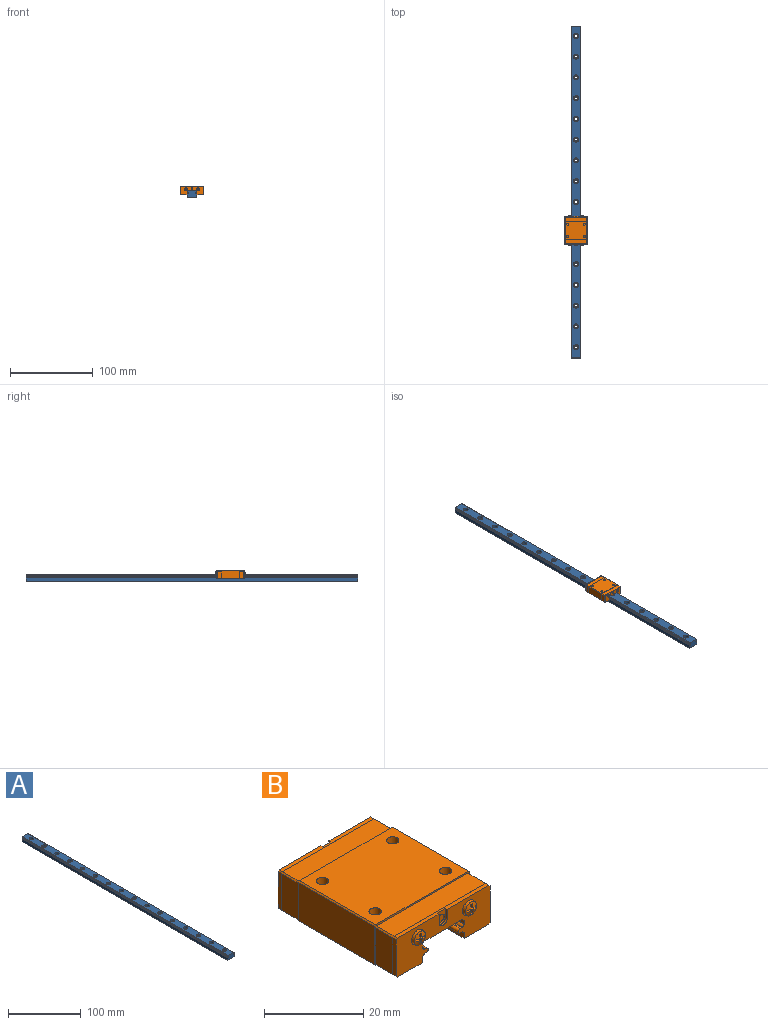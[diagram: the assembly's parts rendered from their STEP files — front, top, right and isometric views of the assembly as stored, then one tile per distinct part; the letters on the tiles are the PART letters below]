
ASSEMBLY  parts=2 mates=1
PART A: 76 faces, bbox 12x400x8 mm
  f0: cylinder r=1.75mm len=5mm, axis (0,0,1), area 55mm2, adj f17,f74
  f1: cylinder r=1.75mm len=5mm, axis (0,0,1), area 55mm2, adj f17,f72
  f2: cylinder r=1.75mm len=5mm, axis (0,0,1), area 55mm2, adj f17,f70
  f3: cylinder r=1.75mm len=5mm, axis (0,0,1), area 55mm2, adj f17,f68
  f4: cylinder r=1.75mm len=5mm, axis (0,0,1), area 55mm2, adj f17,f66
  f5: cylinder r=1.75mm len=5mm, axis (0,0,1), area 55mm2, adj f17,f64
  f6: cylinder r=1.75mm len=5mm, axis (0,0,1), area 55mm2, adj f17,f62
  f7: cylinder r=1.75mm len=5mm, axis (0,0,1), area 55mm2, adj f17,f60
  f8: cylinder r=1.75mm len=5mm, axis (0,0,1), area 55mm2, adj f17,f58
  f9: cylinder r=1.75mm len=5mm, axis (0,0,1), area 55mm2, adj f17,f56
  f10: cylinder r=1.75mm len=5mm, axis (0,0,1), area 55mm2, adj f17,f54
  f11: cylinder r=1.75mm len=5mm, axis (0,0,1), area 55mm2, adj f17,f52
  f12: cylinder r=1.75mm len=5mm, axis (0,0,1), area 55mm2, adj f17,f50
  f13: cylinder r=1.75mm len=5mm, axis (0,0,1), area 55mm2, adj f17,f48
  f14: cylinder r=1.75mm len=5mm, axis (0,0,1), area 55mm2, adj f17,f46
  f15: cylinder r=1.75mm len=5mm, axis (0,0,1), area 55mm2, adj f17,f44
  f16: plane 400x4.32mm, normal (-1,0,0), area 1728.7mm2, adj f17,f32,f33,f43
  f17: plane 400x12mm, normal (0,0,-1), area 4646.1mm2, adj f0,f1,f2,f3,f4,f5,f6,f7
  f18: plane 400x4.32mm, normal (1,0,0), area 1728.7mm2, adj f17,f32,f33,f36
  f19: cylinder r=1.14mm len=400mm, axis (0,1,0), area 250.4mm2, adj f32,f33,f36,f37
  f20: plane 400x0.42mm, normal (0,0,1), area 169.7mm2, adj f21,f32,f33,f37
  f21: cylinder r=0.5mm len=400mm, axis (0,1,0), area 754.1mm2, adj f20,f22,f32,f33
  f22: plane 400x0.42mm, normal (0,0,-1), area 168.4mm2, adj f21,f32,f33,f38
  f23: cylinder r=1.14mm len=400mm, axis (0,1,0), area 250.7mm2, adj f32,f33,f38,f39
  f24: plane 400x0.91mm, normal (1,0,0), area 363.9mm2, adj f32,f33,f35,f39
  f25: plane 400x11mm, normal (0,0,1), area 3947.6mm2, adj f32,f33,f34,f35,f45,f47,f49,f51
  f26: plane 400x0.91mm, normal (-1,0,0), area 363.9mm2, adj f32,f33,f34,f40
  f27: cylinder r=1.14mm len=400mm, axis (0,1,0), area 250.7mm2, adj f32,f33,f40,f41
  f28: plane 400x0.42mm, normal (0,0,-1), area 168.4mm2, adj f29,f32,f33,f41
  f29: cylinder r=0.5mm len=400mm, axis (0,1,0), area 754.1mm2, adj f28,f30,f32,f33
  f30: plane 400x0.42mm, normal (0,0,1), area 169.7mm2, adj f29,f32,f33,f42
  f31: cylinder r=1.14mm len=400mm, axis (0,1,0), area 250.4mm2, adj f32,f33,f42,f43
  f32: plane 12x8mm, normal (0,-1,0), area 91.8mm2, adj f16,f17,f18,f19,f20,f21,f22,f23
  f33: plane 12x8mm, normal (0,1,0), area 91.8mm2, adj f16,f17,f18,f19,f20,f21,f22,f23
  f34: plane 400x0.5mm, normal (-0.71,0,0.71), area 282.8mm2, adj f25,f26,f32,f33
  f35: plane 400x0.5mm, normal (0.71,0,0.71), area 282.8mm2, adj f24,f25,f32,f33
  f36: cylinder r=0.16mm len=400mm, axis (0,1,0), area 67.9mm2, adj f18,f19,f32,f33
  f37: cylinder r=0.16mm len=400mm, axis (0,1,0), area 67.8mm2, adj f19,f20,f32,f33
  f38: cylinder r=0.16mm len=400mm, axis (0,1,0), area 67.9mm2, adj f22,f23,f32,f33
  f39: cylinder r=0.16mm len=400mm, axis (0,1,0), area 67.9mm2, adj f23,f24,f32,f33
  f40: cylinder r=0.16mm len=400mm, axis (0,1,0), area 67.9mm2, adj f26,f27,f32,f33
  f41: cylinder r=0.16mm len=400mm, axis (0,1,0), area 67.9mm2, adj f27,f28,f32,f33
  f42: cylinder r=0.16mm len=400mm, axis (0,1,0), area 67.8mm2, adj f30,f31,f32,f33
  f43: cylinder r=0.16mm len=400mm, axis (0,1,0), area 67.9mm2, adj f16,f31,f32,f33
  f44: plane 6x6mm, normal (0,0,1), area 18.7mm2, adj f15,f45
  f45: cylinder r=3mm len=6mm, axis (0,0,1), area 56.5mm2, adj f25,f44
  f46: plane 6x6mm, normal (0,0,1), area 18.7mm2, adj f14,f47
  f47: cylinder r=3mm len=6mm, axis (0,0,1), area 56.5mm2, adj f25,f46
  f48: plane 6x6mm, normal (0,0,1), area 18.7mm2, adj f13,f49
  f49: cylinder r=3mm len=6mm, axis (0,0,1), area 56.5mm2, adj f25,f48
  f50: plane 6x6mm, normal (0,0,1), area 18.7mm2, adj f12,f51
  f51: cylinder r=3mm len=6mm, axis (0,0,1), area 56.5mm2, adj f25,f50
  f52: plane 6x6mm, normal (0,0,1), area 18.7mm2, adj f11,f53
  f53: cylinder r=3mm len=6mm, axis (0,0,1), area 56.5mm2, adj f25,f52
  f54: plane 6x6mm, normal (0,0,1), area 18.7mm2, adj f10,f55
  f55: cylinder r=3mm len=6mm, axis (0,0,1), area 56.5mm2, adj f25,f54
  f56: plane 6x6mm, normal (0,0,1), area 18.7mm2, adj f9,f57
  f57: cylinder r=3mm len=6mm, axis (0,0,1), area 56.5mm2, adj f25,f56
  f58: plane 6x6mm, normal (0,0,1), area 18.7mm2, adj f8,f59
  f59: cylinder r=3mm len=6mm, axis (0,0,1), area 56.5mm2, adj f25,f58
  f60: plane 6x6mm, normal (0,0,1), area 18.7mm2, adj f7,f61
  f61: cylinder r=3mm len=6mm, axis (0,0,1), area 56.5mm2, adj f25,f60
  f62: plane 6x6mm, normal (0,0,1), area 18.7mm2, adj f6,f63
  f63: cylinder r=3mm len=6mm, axis (0,0,1), area 56.5mm2, adj f25,f62
  f64: plane 6x6mm, normal (0,0,1), area 18.7mm2, adj f5,f65
  f65: cylinder r=3mm len=6mm, axis (0,0,1), area 56.5mm2, adj f25,f64
  f66: plane 6x6mm, normal (0,0,1), area 18.7mm2, adj f4,f67
  f67: cylinder r=3mm len=6mm, axis (0,0,1), area 56.5mm2, adj f25,f66
  f68: plane 6x6mm, normal (0,0,1), area 18.7mm2, adj f3,f69
  f69: cylinder r=3mm len=6mm, axis (0,0,1), area 56.5mm2, adj f25,f68
  f70: plane 6x6mm, normal (0,0,1), area 18.7mm2, adj f2,f71
  f71: cylinder r=3mm len=6mm, axis (0,0,1), area 56.5mm2, adj f25,f70
  f72: plane 6x6mm, normal (0,0,1), area 18.7mm2, adj f1,f73
  f73: cylinder r=3mm len=6mm, axis (0,0,1), area 56.5mm2, adj f25,f72
  f74: plane 6x6mm, normal (0,0,1), area 18.7mm2, adj f0,f75
  f75: cylinder r=3mm len=6mm, axis (0,0,1), area 56.5mm2, adj f25,f74
PART B: 172 faces, bbox 27x35.9x10 mm
  f0: cylinder r=1.25mm len=3.5mm, axis (0,0,-1), area 27.5mm2, adj f1,f158
  f1: cone r=0.62mm half-angle=59deg, axis (0,0,1), area 5.7mm2, adj f0
  f2: cylinder r=1.25mm len=3.5mm, axis (0,0,-1), area 27.5mm2, adj f3,f158
  f3: cone r=0.62mm half-angle=59deg, axis (0,0,1), area 5.7mm2, adj f2
  f4: cylinder r=1.25mm len=3.5mm, axis (0,0,-1), area 27.5mm2, adj f5,f158
  f5: cone r=0.62mm half-angle=59deg, axis (0,0,1), area 5.7mm2, adj f4
  f6: cylinder r=1.25mm len=3.5mm, axis (0,0,-1), area 27.5mm2, adj f7,f158
  f7: cone r=0.62mm half-angle=59deg, axis (0,0,1), area 5.7mm2, adj f6
  f8: cylinder r=0.5mm len=33.7mm, axis (0,1,0), area 63.6mm2, adj f58,f115,f148,f149
  f9: cylinder r=0.5mm len=33.7mm, axis (0,1,0), area 63.6mm2, adj f58,f115,f137,f138
  f10: cylinder r=1.15mm len=2.3mm, axis (0,1,0), area 3.6mm2, adj f114,f124
  f11: cylinder r=1.75mm len=3.5mm, axis (0,1,0), area 5.5mm2, adj f109,f115
  f12: cylinder r=1.75mm len=3.5mm, axis (0,1,0), area 5.5mm2, adj f108,f115
  f13: cone r=0.85mm half-angle=5deg, axis (0,1,0), area 11.5mm2, adj f14,f109
  f14: cone r=0.8mm half-angle=72.7deg, axis (0,1,0), area 6.3mm2, adj f13,f96,f97,f98,f99,f100,f101,f102
  f15: cone r=0.85mm half-angle=5deg, axis (0,1,0), area 11.5mm2, adj f16,f108
  f16: cone r=0.8mm half-angle=72.7deg, axis (0,1,0), area 6.3mm2, adj f15,f83,f84,f85,f86,f87,f88,f89
  f17: cylinder r=1.15mm len=2.3mm, axis (0,-1,0), area 3.6mm2, adj f57,f67
  f18: cylinder r=1.75mm len=3.5mm, axis (0,-1,0), area 5.5mm2, adj f52,f58
  f19: cylinder r=1.75mm len=3.5mm, axis (0,-1,0), area 5.5mm2, adj f51,f58
  f20: cone r=0.85mm half-angle=5deg, axis (0,-1,0), area 11.5mm2, adj f21,f52
  f21: cone r=0.8mm half-angle=72.7deg, axis (0,-1,0), area 6.3mm2, adj f20,f39,f40,f41,f42,f43,f44,f45
  f22: cone r=0.85mm half-angle=5deg, axis (0,-1,0), area 11.5mm2, adj f23,f51
  f23: cone r=0.8mm half-angle=72.7deg, axis (0,-1,0), area 6.3mm2, adj f22,f26,f27,f28,f29,f30,f31,f32
  f24: plane 26.6x9.6mm, normal (0,-1,0), area 0.3mm2, adj f55,f59,f60,f61,f62,f63,f64,f65
  f25: plane 2.4x2.4mm, normal (0,1,0), area 2.1mm2, adj f26,f27,f28,f29,f30,f31,f32,f33
  f26: plane 0.93x0.49mm, normal (0,0,1), area 0.4mm2, adj f23,f25,f29,f31
  f27: plane 0.93x0.49mm, normal (0,0,-1), area 0.4mm2, adj f23,f25,f28,f30
  f28: plane 1.36x1.29mm, normal (-1,0,0), area 1mm2, adj f23,f25,f27,f36
  f29: plane 1.36x1.29mm, normal (-1,0,0), area 1mm2, adj f23,f25,f26,f32
  f30: plane 1.36x1.29mm, normal (1,0,0), area 1mm2, adj f23,f25,f27,f33
  f31: plane 1.36x1.29mm, normal (1,0,0), area 1mm2, adj f23,f25,f26,f34
  f32: plane 1.36x1.29mm, normal (0,0,1), area 1mm2, adj f23,f25,f29,f35
  f33: plane 1.36x1.29mm, normal (0,0,-1), area 1mm2, adj f23,f25,f30,f37
  f34: plane 1.36x1.29mm, normal (0,0,1), area 1mm2, adj f23,f25,f31,f37
  f35: plane 0.93x0.49mm, normal (-1,0,0), area 0.4mm2, adj f23,f25,f32,f36
  f36: plane 1.36x1.29mm, normal (0,0,-1), area 1mm2, adj f23,f25,f28,f35
  f37: plane 0.94x0.49mm, normal (1,0,0), area 0.4mm2, adj f23,f25,f33,f34
  f38: plane 2.4x2.4mm, normal (0,1,0), area 2.1mm2, adj f39,f40,f41,f42,f43,f44,f45,f46
  f39: plane 0.93x0.49mm, normal (0,0,1), area 0.4mm2, adj f21,f38,f42,f44
  f40: plane 0.93x0.49mm, normal (0,0,-1), area 0.4mm2, adj f21,f38,f41,f43
  f41: plane 1.36x1.29mm, normal (-1,0,0), area 1mm2, adj f21,f38,f40,f49
  f42: plane 1.36x1.29mm, normal (-1,0,0), area 1mm2, adj f21,f38,f39,f45
  f43: plane 1.36x1.29mm, normal (1,0,0), area 1mm2, adj f21,f38,f40,f46
  f44: plane 1.36x1.29mm, normal (1,0,0), area 1mm2, adj f21,f38,f39,f47
  f45: plane 1.36x1.29mm, normal (0,0,1), area 1mm2, adj f21,f38,f42,f48
  f46: plane 1.36x1.29mm, normal (0,0,-1), area 1mm2, adj f21,f38,f43,f50
  f47: plane 1.36x1.29mm, normal (0,0,1), area 1mm2, adj f21,f38,f44,f50
  f48: plane 0.93x0.49mm, normal (-1,0,0), area 0.4mm2, adj f21,f38,f45,f49
  f49: plane 1.36x1.29mm, normal (0,0,-1), area 1mm2, adj f21,f38,f41,f48
  f50: plane 0.94x0.49mm, normal (1,0,0), area 0.4mm2, adj f21,f38,f46,f47
  f51: plane 3.5x3.5mm, normal (0,1,0), area 0.5mm2, adj f19,f22
  f52: plane 3.5x3.5mm, normal (0,1,0), area 0.5mm2, adj f18,f20
  f53: plane 2.1x0.5mm, normal (1,0,0), area 1.1mm2, adj f55,f56,f57,f58
  f54: plane 2.1x0.5mm, normal (-1,0,0), area 1.1mm2, adj f55,f56,f57,f58
  f55: plane 26x1mm, normal (0,0,1), area 24.8mm2, adj f24,f53,f54,f57,f58,f62,f63
  f56: cylinder r=1.2mm len=2.4mm, axis (0,-1,0), area 1.9mm2, adj f53,f54,f57,f58
  f57: plane 3.3x2.4mm, normal (0,1,0), area 3.1mm2, adj f17,f53,f54,f55,f56
  f58: plane 26.6x9.6mm, normal (0,1,0), area 172.9mm2, adj f8,f9,f18,f19,f53,f54,f55,f56
  f59: plane 7x1mm, normal (0,0,-1), area 7mm2, adj f24,f58,f65,f134
  f60: plane 7x1mm, normal (0,0,-1), area 7mm2, adj f24,f58,f66,f152
  f61: plane 9x1mm, normal (1,0,0), area 9mm2, adj f24,f58,f62,f66
  f62: plane 1x0.3mm, normal (0.71,0,0.71), area 0.4mm2, adj f24,f55,f58,f61
  f63: plane 1x0.3mm, normal (-0.71,0,0.71), area 0.4mm2, adj f24,f55,f58,f64
  f64: plane 9x1mm, normal (-1,0,0), area 9mm2, adj f24,f58,f63,f65
  f65: plane 1x0.3mm, normal (-0.71,0,-0.71), area 0.4mm2, adj f24,f58,f59,f64
  f66: plane 1x0.3mm, normal (0.71,0,-0.71), area 0.4mm2, adj f24,f58,f60,f61
  f67: plane 2.3x2.3mm, normal (0,1,0), area 4.2mm2, adj f17
  f68: cylinder r=1.14mm len=33.7mm, axis (0,-1,0), area 21.1mm2, adj f58,f115,f150,f151
  f69: cylinder r=1.14mm len=33.7mm, axis (0,-1,0), area 21.1mm2, adj f58,f115,f146,f147
  f70: cylinder r=1.14mm len=33.7mm, axis (0,-1,0), area 21.1mm2, adj f58,f115,f139,f140
  f71: cylinder r=1.14mm len=33.7mm, axis (0,-1,0), area 21.1mm2, adj f58,f115,f135,f136
  f72: plane 7x5mm, normal (0,0,-1), area 35mm2, adj f24,f79,f134,f163
  f73: plane 7x5mm, normal (0,0,-1), area 35mm2, adj f24,f80,f152,f163
  f74: plane 8.99x5mm, normal (1,0,0), area 45mm2, adj f24,f75,f80,f163
  f75: plane 5x0.3mm, normal (0.71,0,0.71), area 2.1mm2, adj f24,f74,f76,f163
  f76: plane 25.99x5mm, normal (0,0,1), area 130mm2, adj f24,f75,f77,f163
  f77: plane 5x0.3mm, normal (-0.71,0,0.71), area 2.1mm2, adj f24,f76,f78,f163
  f78: plane 8.99x5mm, normal (-1,0,0), area 45mm2, adj f24,f77,f79,f163
  f79: plane 5x0.3mm, normal (-0.71,0,-0.71), area 2.1mm2, adj f24,f72,f78,f163
  f80: plane 5x0.3mm, normal (0.71,0,-0.71), area 2.1mm2, adj f24,f73,f74,f163
  f81: plane 26.6x9.6mm, normal (0,1,0), area 0.3mm2, adj f112,f116,f117,f118,f119,f120,f121,f122
  f82: plane 2.4x2.4mm, normal (0,-1,0), area 2.1mm2, adj f83,f84,f85,f86,f87,f88,f89,f90
  f83: plane 0.93x0.49mm, normal (0,0,1), area 0.4mm2, adj f16,f82,f86,f88
  f84: plane 0.93x0.49mm, normal (0,0,-1), area 0.4mm2, adj f16,f82,f85,f87
  f85: plane 1.36x1.29mm, normal (1,0,0), area 1mm2, adj f16,f82,f84,f93
  f86: plane 1.36x1.29mm, normal (1,0,0), area 1mm2, adj f16,f82,f83,f89
  f87: plane 1.36x1.29mm, normal (-1,0,0), area 1mm2, adj f16,f82,f84,f90
  f88: plane 1.36x1.29mm, normal (-1,0,0), area 1mm2, adj f16,f82,f83,f91
  f89: plane 1.36x1.29mm, normal (0,0,1), area 1mm2, adj f16,f82,f86,f92
  f90: plane 1.36x1.29mm, normal (0,0,-1), area 1mm2, adj f16,f82,f87,f94
  f91: plane 1.36x1.29mm, normal (0,0,1), area 1mm2, adj f16,f82,f88,f94
  f92: plane 0.93x0.49mm, normal (1,0,0), area 0.4mm2, adj f16,f82,f89,f93
  f93: plane 1.36x1.29mm, normal (0,0,-1), area 1mm2, adj f16,f82,f85,f92
  f94: plane 0.94x0.49mm, normal (-1,0,0), area 0.4mm2, adj f16,f82,f90,f91
  f95: plane 2.4x2.4mm, normal (0,-1,0), area 2.1mm2, adj f96,f97,f98,f99,f100,f101,f102,f103
  f96: plane 0.93x0.49mm, normal (0,0,1), area 0.4mm2, adj f14,f95,f99,f101
  f97: plane 0.93x0.49mm, normal (0,0,-1), area 0.4mm2, adj f14,f95,f98,f100
  f98: plane 1.36x1.29mm, normal (1,0,0), area 1mm2, adj f14,f95,f97,f106
  f99: plane 1.36x1.29mm, normal (1,0,0), area 1mm2, adj f14,f95,f96,f102
  f100: plane 1.36x1.29mm, normal (-1,0,0), area 1mm2, adj f14,f95,f97,f103
  f101: plane 1.36x1.29mm, normal (-1,0,0), area 1mm2, adj f14,f95,f96,f104
  f102: plane 1.36x1.29mm, normal (0,0,1), area 1mm2, adj f14,f95,f99,f105
  f103: plane 1.36x1.29mm, normal (0,0,-1), area 1mm2, adj f14,f95,f100,f107
  f104: plane 1.36x1.29mm, normal (0,0,1), area 1mm2, adj f14,f95,f101,f107
  f105: plane 0.93x0.49mm, normal (1,0,0), area 0.4mm2, adj f14,f95,f102,f106
  f106: plane 1.36x1.29mm, normal (0,0,-1), area 1mm2, adj f14,f95,f98,f105
  f107: plane 0.94x0.49mm, normal (-1,0,0), area 0.4mm2, adj f14,f95,f103,f104
  f108: plane 3.5x3.5mm, normal (0,-1,0), area 0.5mm2, adj f12,f15
  f109: plane 3.5x3.5mm, normal (0,-1,0), area 0.5mm2, adj f11,f13
  f110: plane 2.1x0.5mm, normal (-1,0,0), area 1mm2, adj f112,f113,f114,f115
  f111: plane 2.1x0.5mm, normal (1,0,0), area 1mm2, adj f112,f113,f114,f115
  f112: plane 26x1mm, normal (0,0,1), area 24.8mm2, adj f81,f110,f111,f114,f115,f119,f120
  f113: cylinder r=1.2mm len=2.4mm, axis (0,1,0), area 1.9mm2, adj f110,f111,f114,f115
  f114: plane 3.3x2.4mm, normal (0,-1,0), area 3.1mm2, adj f10,f110,f111,f112,f113
  f115: plane 26.6x9.6mm, normal (0,-1,0), area 172.9mm2, adj f8,f9,f11,f12,f68,f69,f70,f71
  f116: plane 7x1mm, normal (0,0,-1), area 7mm2, adj f81,f115,f122,f152
  f117: plane 7x1mm, normal (0,0,-1), area 7mm2, adj f81,f115,f123,f134
  f118: plane 9x1mm, normal (-1,0,0), area 9mm2, adj f81,f115,f119,f123
  f119: plane 1x0.3mm, normal (-0.71,0,0.71), area 0.4mm2, adj f81,f112,f115,f118
  f120: plane 1x0.3mm, normal (0.71,0,0.71), area 0.4mm2, adj f81,f112,f115,f121
  f121: plane 9x1mm, normal (1,0,0), area 9mm2, adj f81,f115,f120,f122
  f122: plane 1x0.3mm, normal (0.71,0,-0.71), area 0.4mm2, adj f81,f115,f116,f121
  f123: plane 1x0.3mm, normal (-0.71,0,-0.71), area 0.4mm2, adj f81,f115,f117,f118
  f124: plane 2.3x2.3mm, normal (0,-1,0), area 4.2mm2, adj f10
  f125: plane 7x5mm, normal (0,0,-1), area 35mm2, adj f81,f132,f152,f153
  f126: plane 7x5mm, normal (0,0,-1), area 35mm2, adj f81,f133,f134,f153
  f127: plane 8.99x5mm, normal (-1,0,0), area 44.9mm2, adj f81,f128,f133,f153
  f128: plane 5x0.3mm, normal (-0.71,0,0.71), area 2.1mm2, adj f81,f127,f129,f153
  f129: plane 25.99x5mm, normal (0,0,1), area 129.9mm2, adj f81,f128,f130,f153
  f130: plane 5x0.3mm, normal (0.71,0,0.71), area 2.1mm2, adj f81,f129,f131,f153
  f131: plane 8.99x5mm, normal (1,0,0), area 45mm2, adj f81,f130,f132,f153
  f132: plane 5x0.3mm, normal (0.71,0,-0.71), area 2.1mm2, adj f81,f125,f131,f153
  f133: plane 5x0.3mm, normal (-0.71,0,-0.71), area 2.1mm2, adj f81,f126,f127,f153
  f134: plane 33.7x1.32mm, normal (1,0,0), area 44.5mm2, adj f24,f58,f59,f72,f81,f115,f117,f126
  f135: cylinder r=0.16mm len=33.7mm, axis (0,1,0), area 5.7mm2, adj f58,f71,f115,f134
  f136: cylinder r=0.16mm len=33.7mm, axis (0,1,0), area 5.7mm2, adj f58,f71,f115,f137
  f137: plane 33.7x0.42mm, normal (0,0,-1), area 14.2mm2, adj f9,f58,f115,f136
  f138: plane 33.7x0.42mm, normal (0,0,1), area 14.2mm2, adj f9,f58,f115,f139
  f139: cylinder r=0.16mm len=33.7mm, axis (0,1,0), area 5.7mm2, adj f58,f70,f115,f138
  f140: cylinder r=0.16mm len=33.7mm, axis (0,1,0), area 5.7mm2, adj f58,f70,f115,f141
  f141: plane 33.7x0.82mm, normal (1,0,0), area 27.7mm2, adj f58,f115,f140,f142
  f142: plane 33.7x0.59mm, normal (0.76,0,-0.65), area 26mm2, adj f58,f115,f141,f143
  f143: plane 33.7x11mm, normal (0,0,-1), area 370.7mm2, adj f58,f115,f142,f144
  f144: plane 33.7x0.59mm, normal (-0.76,0,-0.65), area 26mm2, adj f58,f115,f143,f145
  f145: plane 33.7x0.82mm, normal (-1,0,0), area 27.7mm2, adj f58,f115,f144,f146
  f146: cylinder r=0.16mm len=33.7mm, axis (0,1,0), area 5.7mm2, adj f58,f69,f115,f145
  f147: cylinder r=0.16mm len=33.7mm, axis (0,1,0), area 5.7mm2, adj f58,f69,f115,f148
  f148: plane 33.7x0.42mm, normal (0,0,1), area 14.2mm2, adj f8,f58,f115,f147
  f149: plane 33.7x0.42mm, normal (0,0,-1), area 14.2mm2, adj f8,f58,f115,f150
  f150: cylinder r=0.16mm len=33.7mm, axis (0,1,0), area 5.7mm2, adj f58,f68,f115,f149
  f151: cylinder r=0.16mm len=33.7mm, axis (0,1,0), area 5.7mm2, adj f58,f68,f115,f152
  f152: plane 33.7x1.32mm, normal (-1,0,0), area 44.5mm2, adj f24,f58,f60,f73,f81,f115,f116,f125
  f153: plane 27x10mm, normal (0,-1,0), area 14.9mm2, adj f125,f126,f127,f128,f129,f130,f131,f132
  f154: plane 21.7x7.2mm, normal (0,0,-1), area 156.2mm2, adj f152,f153,f161,f163
  f155: plane 21.7x7.2mm, normal (0,0,-1), area 156.2mm2, adj f134,f153,f162,f163
  f156: plane 21.7x9.4mm, normal (-1,0,0), area 204mm2, adj f153,f157,f162,f163
  f157: plane 21.7x0.3mm, normal (-0.71,0,0.71), area 9.2mm2, adj f153,f156,f158,f163
  f158: plane 26.4x21.7mm, normal (0,0,1), area 553.2mm2, adj f0,f2,f4,f6,f153,f157,f159,f163
  f159: plane 21.7x0.3mm, normal (0.71,0,0.71), area 9.2mm2, adj f153,f158,f160,f163
  f160: plane 21.7x9.4mm, normal (1,0,0), area 204mm2, adj f153,f159,f161,f163
  f161: plane 21.7x0.3mm, normal (0.71,0,-0.71), area 9.2mm2, adj f153,f154,f160,f163
  f162: plane 21.7x0.3mm, normal (-0.71,0,-0.71), area 9.2mm2, adj f153,f155,f156,f163
  f163: plane 27x10mm, normal (0,1,0), area 14.9mm2, adj f72,f73,f74,f75,f76,f77,f78,f79
  f164: cone r=0.5mm half-angle=17.1deg, axis (0,-1,0), area 2.7mm2, adj f166,f167
  f165: cylinder r=1.25mm len=2.5mm, axis (0,-1,0), area 3.9mm2, adj f166,f167
  f166: plane 2.5x2.5mm, normal (0,1,0), area 2.3mm2, adj f164,f165
  f167: plane 2.5x2.5mm, normal (0,-1,0), area 3.1mm2, adj f164,f165
  f168: cylinder r=1.25mm len=2.5mm, axis (0,-1,0), area 3.9mm2, adj f170,f171
  f169: cone r=0.5mm half-angle=17.1deg, axis (0,-1,0), area 2.7mm2, adj f170,f171
  f170: plane 2.5x2.5mm, normal (0,-1,0), area 3.1mm2, adj f168,f169
  f171: plane 2.5x2.5mm, normal (0,1,0), area 2.3mm2, adj f168,f169
PLACE A t=(-199.02,610.43,213.47)mm
PLACE B t=(-205.02,347.18,213.47)mm
MATE slider A.f21 <-> B.f8  axis (0,-1,0) through (-200.25,210.43,218.93)mm
